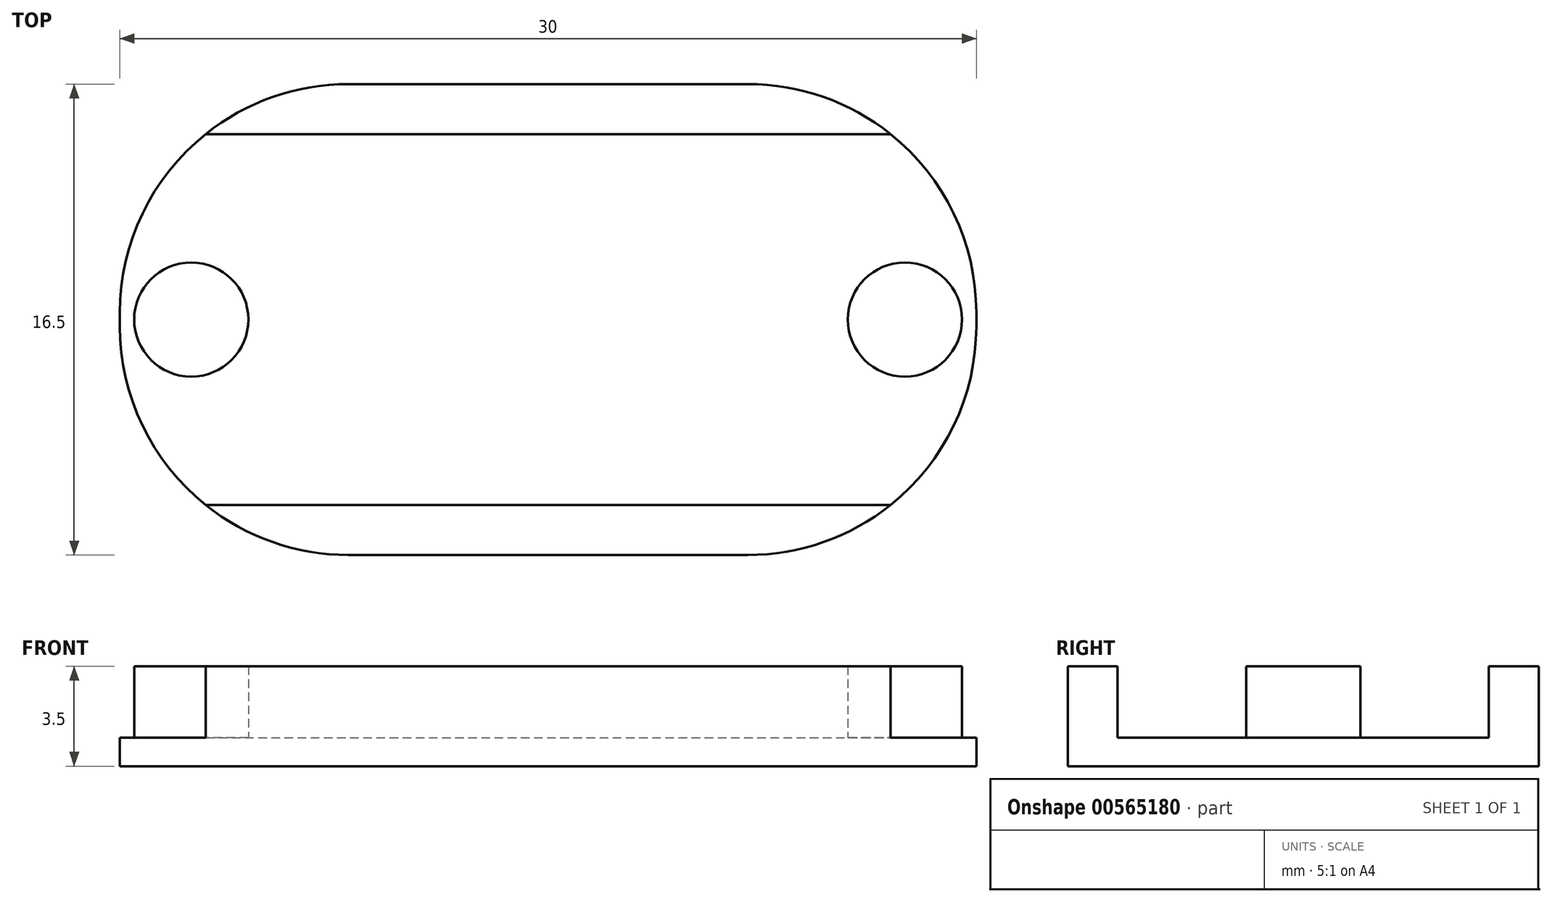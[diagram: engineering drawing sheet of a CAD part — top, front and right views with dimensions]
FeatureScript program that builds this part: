
annotation { "Feature Type Name" : "Feature", "Feature Type Description" : "" }
export const myFeature = defineFeature(function(context is Context, id is Id, definition is map)
    precondition{}
    {
        {
            var Q0;
            Q0=qCreatedBy(makeId("Top.planeOp"),FACE);
            var sketch = newSketch(context, id + "F0", { "sketchPlane" : qUnion([Q0])});
            skLineSegment(sketch, "E0.bottom", {"start": v(15, 8.25) * mm, "end": v(-15, 8.25) * mm});
            skLineSegment(sketch, "E0.top", {"start": v(15, -8.25) * mm, "end": v(-15, -8.25) * mm});
            skLineSegment(sketch, "E0.left", {"start": v(15, 8.25) * mm, "end": v(15, -8.25) * mm});
            skLineSegment(sketch, "E0.right", {"start": v(-15, 8.25) * mm, "end": v(-15, -8.25) * mm});
            skPoint(sketch, "E0.middle", {"position": v(0, 0) * mm});
            skLineSegment(sketch, "E1", {"start": v(-18.94, 0) * mm, "end": v(22.91, 0) * mm, "construction": true});
            skCircle(sketch, "E2", {"center": v(-12.5, 0) * mm, "radius": 2 * mm});
            skCircle(sketch, "E3", {"center": v(12.5, 0) * mm, "radius": 2 * mm});
            skSolve(sketch);
        }
        {
            var Q0;
            Q0=makeQuery(id+"F0.imprint","IMPRINT",FACE,{"disambiguationData":[TD([[makeQuery(id+"F0.imprint","IMPRINT",EDGE,{"derivedFrom":sQuery(id+"F0.wireOp",EDGE,"E0.bottom")}),1.0]])]});
            var Q1;
            Q1=makeQuery(id+"F0.imprint","IMPRINT",FACE,{"disambiguationData":[TD([[makeQuery(id+"F0.imprint","IMPRINT",EDGE,{"derivedFrom":sQuery(id+"F0.wireOp",EDGE,"E2")}),1.0]])]});
            var Q2;
            Q2=makeQuery(id+"F0.imprint","IMPRINT",FACE,{"disambiguationData":[TD([[makeQuery(id+"F0.imprint","IMPRINT",EDGE,{"derivedFrom":sQuery(id+"F0.wireOp",EDGE,"E3")}),1.0]])]});
            extrude(context, id + "F1", {"entities" : qUnion([Q0, Q1, Q2]), "depth" : 1 * mm, "offsetDistance" : 25 * mm});
        }
        {
            var Q0;
            Q0=makeQuery(id+"F0.imprint","IMPRINT",FACE,{"disambiguationData":[TD([[makeQuery(id+"F0.imprint","IMPRINT",EDGE,{"derivedFrom":sQuery(id+"F0.wireOp",EDGE,"E2")}),1.0]])]});
            var Q1;
            Q1=makeQuery(id+"F0.imprint","IMPRINT",FACE,{"disambiguationData":[TD([[makeQuery(id+"F0.imprint","IMPRINT",EDGE,{"derivedFrom":sQuery(id+"F0.wireOp",EDGE,"E3")}),1.0]])]});
            var Q2;
            Q2=sQuery(id+"F0.wireOp",EDGE,"E2");
            var Q3;
            Q3=sQuery(id+"F0.wireOp",EDGE,"E3");
            extrude(context, id + "F2", {"entities" : qUnion([Q0, Q1]), "operationType" : NewBodyOperationType.ADD, "surfaceEntities" : qUnion([Q2, Q3]), "depth" : 3.5 * mm, "offsetDistance" : 25 * mm});
        }
        {
            var Q0;
            Q0=makeQuery(id+"F1.opExtrude","CAP_FACE",FACE,{"disambiguationData":[OSD([sQuery(id+"F0.wireOp",EDGE,"E0.bottom"),sQuery(id+"F0.wireOp",EDGE,"E0.top"),sQuery(id+"F0.wireOp",EDGE,"E0.left"),sQuery(id+"F0.wireOp",EDGE,"E0.right")])],"isStart":false});
            var sketch = newSketch(context, id + "F3", { "sketchPlane" : qUnion([Q0])});
            skLineSegment(sketch, "E4.bottom", {"start": v(-15, 8.25) * mm, "end": v(15, 8.25) * mm});
            skLineSegment(sketch, "E4.top", {"start": v(-15, 6.5) * mm, "end": v(15, 6.5) * mm});
            skLineSegment(sketch, "E4.left", {"start": v(-15, 8.25) * mm, "end": v(-15, 6.5) * mm});
            skLineSegment(sketch, "E4.right", {"start": v(15, 8.25) * mm, "end": v(15, 6.5) * mm});
            skLineSegment(sketch, "E5", {"start": v(-15, 0) * mm, "end": v(15, 0) * mm, "construction": true});
            skLineSegment(sketch, "E6.MirrorCS", {"start": v(-15, -6.5) * mm, "end": v(15, -6.5) * mm});
            skLineSegment(sketch, "E7.MirrorCS", {"start": v(-15, -8.25) * mm, "end": v(-15, -6.5) * mm});
            skLineSegment(sketch, "E8.MirrorCS", {"start": v(-15, -8.25) * mm, "end": v(15, -8.25) * mm});
            skLineSegment(sketch, "E9.MirrorCS", {"start": v(15, -8.25) * mm, "end": v(15, -6.5) * mm});
            skSolve(sketch);
        }
        {
            var Q0;
            Q0 = qSketchRegion(id + "F3", true);
            extrude(context, id + "F4", {"entities" : qUnion([Q0]), "operationType" : NewBodyOperationType.ADD, "depth" : 2.5 * mm, "offsetDistance" : 25 * mm});
        }
        {
            var Q0;
            Q0=makeQuery(id+"F4.boolean.opBoolean","MERGE",EDGE,{"derivedFrom":[makeQuery(id+"F1.opExtrude","SWEPT_EDGE",EDGE,{"disambiguationData":[OSD([sQuery(id+"F0.wireOp",EDGE,"E0.top"),sQuery(id+"F0.wireOp",EDGE,"E0.right")])]}),makeQuery(id+"F4.opExtrude","SWEPT_EDGE",EDGE,{"disambiguationData":[OSD([sQuery(id+"F3.wireOp",EDGE,"E7.MirrorCS"),sQuery(id+"F3.wireOp",EDGE,"E8.MirrorCS")])]})]});
            var Q1;
            Q1=makeQuery(id+"F4.boolean.opBoolean","MERGE",EDGE,{"derivedFrom":[makeQuery(id+"F1.opExtrude","SWEPT_EDGE",EDGE,{"disambiguationData":[OSD([sQuery(id+"F0.wireOp",EDGE,"E0.bottom"),sQuery(id+"F0.wireOp",EDGE,"E0.right")])]}),makeQuery(id+"F4.opExtrude","SWEPT_EDGE",EDGE,{"disambiguationData":[OSD([sQuery(id+"F3.wireOp",EDGE,"E4.bottom"),sQuery(id+"F3.wireOp",EDGE,"E4.left")])]})]});
            var Q2;
            Q2=makeQuery(id+"F4.boolean.opBoolean","MERGE",EDGE,{"derivedFrom":[makeQuery(id+"F1.opExtrude","SWEPT_EDGE",EDGE,{"disambiguationData":[OSD([sQuery(id+"F0.wireOp",EDGE,"E0.top"),sQuery(id+"F0.wireOp",EDGE,"E0.left")])]}),makeQuery(id+"F4.opExtrude","SWEPT_EDGE",EDGE,{"disambiguationData":[OSD([sQuery(id+"F3.wireOp",EDGE,"E8.MirrorCS"),sQuery(id+"F3.wireOp",EDGE,"E9.MirrorCS")])]})]});
            var Q3;
            Q3=makeQuery(id+"F4.boolean.opBoolean","MERGE",EDGE,{"derivedFrom":[makeQuery(id+"F1.opExtrude","SWEPT_EDGE",EDGE,{"disambiguationData":[OSD([sQuery(id+"F0.wireOp",EDGE,"E0.bottom"),sQuery(id+"F0.wireOp",EDGE,"E0.left")])]}),makeQuery(id+"F4.opExtrude","SWEPT_EDGE",EDGE,{"disambiguationData":[OSD([sQuery(id+"F3.wireOp",EDGE,"E4.bottom"),sQuery(id+"F3.wireOp",EDGE,"E4.right")])]})]});
            fillet(context, id + "F5", {"entities" : qUnion([Q0, Q1, Q2, Q3]), "radius" : 8 * mm, "tangentPropagation" : true, "allowEdgeOverflow" : false});
        }
    });
